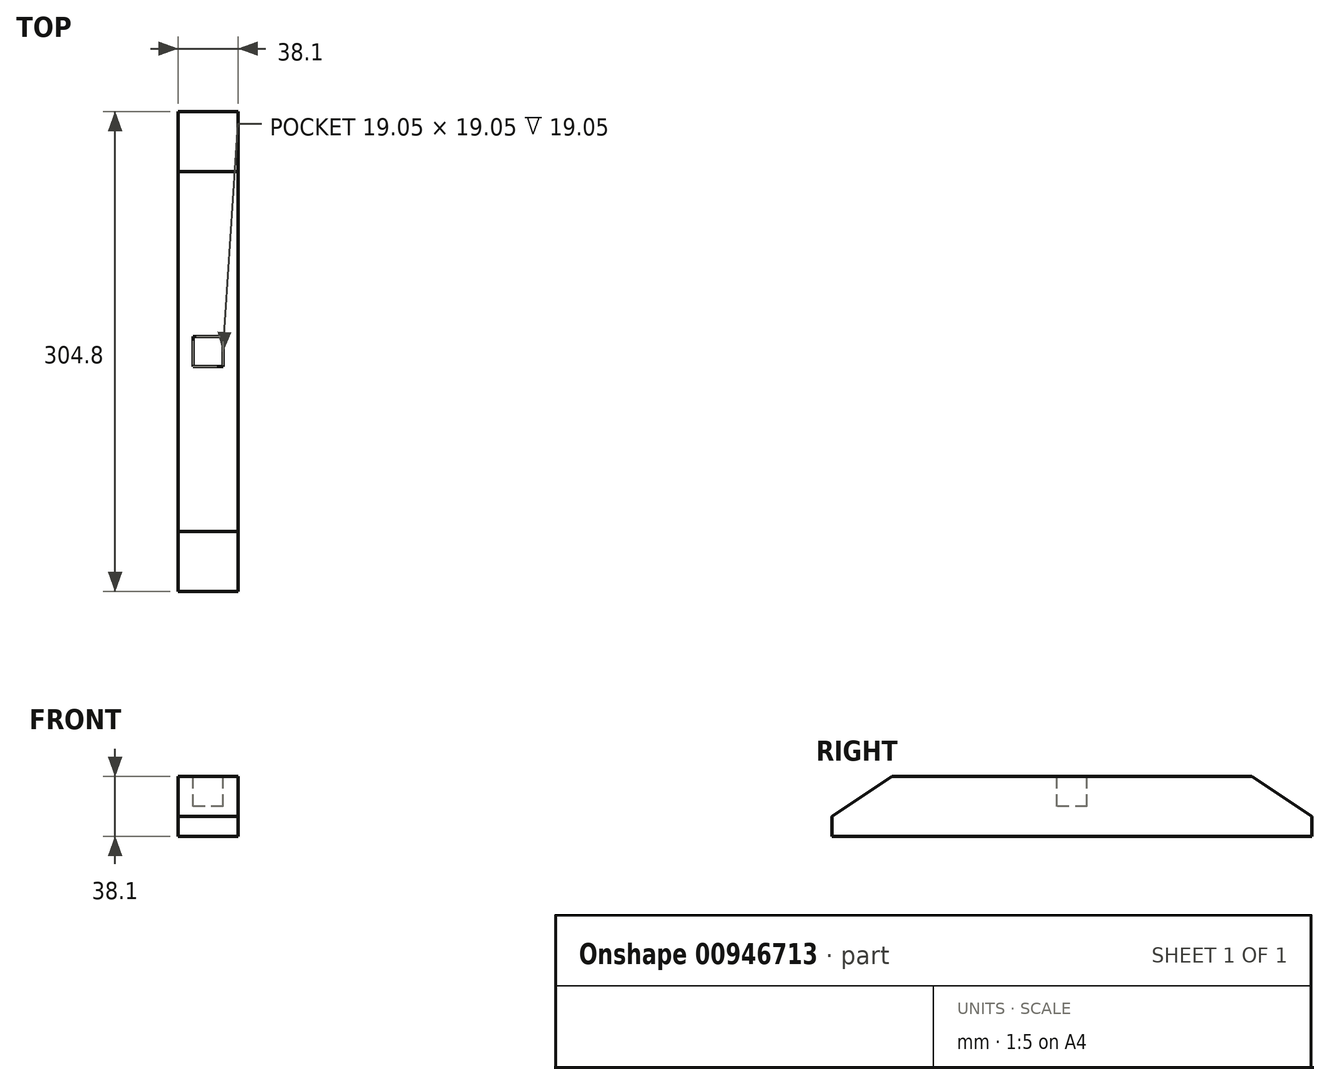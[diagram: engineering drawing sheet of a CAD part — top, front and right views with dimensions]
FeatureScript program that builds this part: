
annotation { "Feature Type Name" : "Feature", "Feature Type Description" : "" }
export const myFeature = defineFeature(function(context is Context, id is Id, definition is map)
    precondition{}
    {
        {
            var Q0;
            Q0=qCreatedBy(makeId("Right.planeOp"),FACE);
            var sketch = newSketch(context, id + "F0", { "sketchPlane" : qUnion([Q0])});
            skLineSegment(sketch, "E0.bottom", {"start": v(114.3, 19.05) * mm, "end": v(-114.3, 19.05) * mm});
            skLineSegment(sketch, "E0.top", {"start": v(152.4, -19.05) * mm, "end": v(76.2, -19.05) * mm});
            skLineSegment(sketch, "E0.left", {"start": v(152.4, -6.35) * mm, "end": v(152.4, -19.05) * mm});
            skLineSegment(sketch, "E0.right", {"start": v(-152.4, -6.35) * mm, "end": v(-152.4, -19.05) * mm});
            skPoint(sketch, "E0.middle", {"position": v(0, 0) * mm});
            skLineSegment(sketch, "E1", {"start": v(152.4, -19.05) * mm, "end": v(152.4, -6.35) * mm});
            skLineSegment(sketch, "E2", {"start": v(152.4, -6.35) * mm, "end": v(114.3, 19.05) * mm});
            skLineSegment(sketch, "E3.MirrorCS", {"start": v(-152.4, -6.35) * mm, "end": v(-114.3, 19.05) * mm});
            skLineSegment(sketch, "E4.left", {"start": v(76.2, -19.05) * mm, "end": v(76.2, -25.4) * mm});
            skPoint(sketch, "E4.middle", {"position": v(0, -19.05) * mm});
            skPoint(sketch, "E5.orphan", {"position": v(-152.4, 19.05) * mm});
            skPoint(sketch, "E6.orphan", {"position": v(-76.2, -25.4) * mm});
            skLineSegment(sketch, "E7.trimOffspring", {"start": v(-101.6, -19.05) * mm, "end": v(-152.4, -19.05) * mm});
            skPoint(sketch, "E8.orphan", {"position": v(152.4, 19.05) * mm});
            skLineSegment(sketch, "E9", {"start": v(-101.6, -19.05) * mm, "end": v(76.2, -19.05) * mm});
            skPoint(sketch, "E4.right.start.orphan", {"position": v(-76.2, -12.7) * mm});
            skPoint(sketch, "E10.orphan", {"position": v(76.2, -12.7) * mm});
            skSolve(sketch);
        }
        {
            var Q0;
            Q0=qSketchRegion(id+"F0",true);
            extrude(context, id + "F1", {"entities" : qUnion([Q0]), "depth" : 38.1 * mm, "offsetDistance" : 25.4 * mm});
        }
        {
            var Q0;
            Q0=makeQuery(id+"F1.opExtrude","SWEPT_FACE",FACE,{"disambiguationData":[OSD([sQuery(id+"F0.wireOp",EDGE,"E0.bottom")])]});
            var sketch = newSketch(context, id + "F2", { "sketchPlane" : qUnion([Q0])});
            skLineSegment(sketch, "E11", {"start": v(0, 0) * mm, "end": v(38.1, 0) * mm});
            skLineSegment(sketch, "E12.bottom", {"start": v(28.58, 9.53) * mm, "end": v(9.52, 9.53) * mm});
            skLineSegment(sketch, "E12.top", {"start": v(28.58, -9.52) * mm, "end": v(9.53, -9.52) * mm});
            skLineSegment(sketch, "E12.left", {"start": v(28.58, 9.53) * mm, "end": v(28.58, -9.52) * mm});
            skLineSegment(sketch, "E12.right", {"start": v(9.52, 9.53) * mm, "end": v(9.52, -9.52) * mm});
            skPoint(sketch, "E12.middle", {"position": v(19.05, 0) * mm});
            skSolve(sketch);
        }
        {
            var Q0;
            Q0=qSketchRegion(id+"F2",true);
            extrude(context, id + "F3", {"entities" : qUnion([Q0]), "operationType" : NewBodyOperationType.REMOVE, "oppositeDirection" : true, "depth" : 19.05 * mm, "offsetDistance" : 25.4 * mm});
        }
        {
            var Q0;
            Q0=makeQuery(id+"F1.opExtrude","SWEPT_BODY",BODY,{"disambiguationData":[OSD([sQuery(id+"F0.wireOp",EDGE,"E0.bottom"),sQuery(id+"F0.wireOp",EDGE,"E0.top"),sQuery(id+"F0.wireOp",EDGE,"E0.right"),sQuery(id+"F0.wireOp",EDGE,"E1"),sQuery(id+"F0.wireOp",EDGE,"E2"),sQuery(id+"F0.wireOp",EDGE,"E3.MirrorCS"),sQuery(id+"F0.wireOp",EDGE,"E4.bottom"),sQuery(id+"F0.wireOp",EDGE,"E4.left"),sQuery(id+"F0.wireOp",EDGE,"E4.right"),sQuery(id+"F0.wireOp",EDGE,"E7.trimOffspring")])]});
            transform(context, id + "F4", {"entities" : qUnion([Q0]), "transformType" : TransformType.TRANSLATION_3D, "dx" : 0 * mm, "dy" : 0 * mm, "dz" : 0 * mm, "makeCopy" : true});
        }
        {
            var Q0;
            Q0=makeQuery(id+"F4.opPattern","COPY",BODY,{"derivedFrom":makeQuery(id+"F1.opExtrude","SWEPT_BODY",BODY,{"disambiguationData":[OSD([sQuery(id+"F0.wireOp",EDGE,"E0.bottom"),sQuery(id+"F0.wireOp",EDGE,"E0.top"),sQuery(id+"F0.wireOp",EDGE,"E0.right"),sQuery(id+"F0.wireOp",EDGE,"E1"),sQuery(id+"F0.wireOp",EDGE,"E2"),sQuery(id+"F0.wireOp",EDGE,"E3.MirrorCS"),sQuery(id+"F0.wireOp",EDGE,"E4.bottom"),sQuery(id+"F0.wireOp",EDGE,"E4.left"),sQuery(id+"F0.wireOp",EDGE,"E4.right"),sQuery(id+"F0.wireOp",EDGE,"E7.trimOffspring")])]}),"instanceName":"1"});
            deleteBodies(context, id + "F5", {"entities" : qUnion([Q0])});
        }
    });
